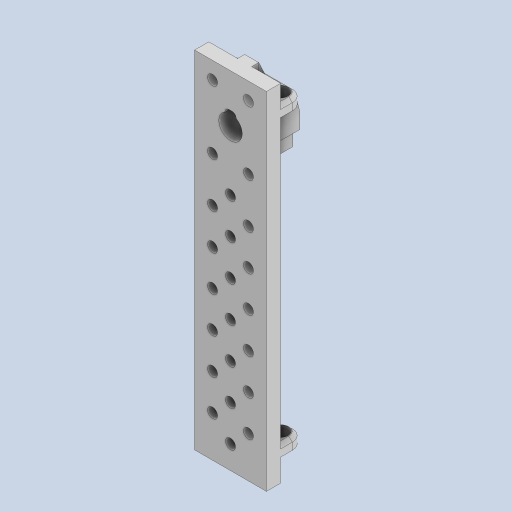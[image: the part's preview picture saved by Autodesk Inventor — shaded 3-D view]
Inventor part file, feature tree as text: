
AUTODESK INVENTOR PART (.ipt)
format: ipt  version: 2024 (Build 280153000, 153)  size: 1,131,520 bytes
history: native  units: mm
features: projected_geometry x31, extrude x23, sketch x19, plane x4, mirror x2, other x2, chamfer x1, loft x1
ambient origin geometry x8: Origin, YZ Plane, XZ Plane, XY Plane, X Axis, Y Axis, Z Axis, Center Point
bodies: Solid1 (feature_tree)
feature tree (83):
  extrude  "Extrusion1"  Depth=10.0mm
  extrude  "Extrusion2"  Depth=16.002mm
  extrude  "Extrusion3"  Depth=16.002mm
  plane  "Work Plane5"
  mirror  "Mirror1"
  extrude  "Extrusion4"  Depth=5.5118mm
  extrude  "Extrusion22"  Depth=2.9972mm
  extrude  "Extrusion23"  Depth=8.001mm
  extrude  "Extrusion24"  Depth=152.5mm
  extrude  "Extrusion14"  Depth=215.0mm
  plane  "Work Plane2"
  extrude  "Extrusion25"  Depth=8.25mm
  chamfer  "Chamfer1"  Distance=1.0mm
  plane  "Work Plane3"
  loft  "Loft6"
  extrude  "Extrusion27"  Depth=10.0mm
  extrude  "Extrusion28"  Depth=10.0mm
  extrude  "Extrusion29"  Depth=10.0mm
  plane  "Work Plane4"
  extrude  "Extrusion30"  Depth=10.0mm
  extrude  "Extrusion31"  Depth=10.0mm
  extrude  "Extrusion32"  Depth=10.0mm
  extrude  "Extrusion33"  Depth=10.0mm
  extrude  "Extrusion34"  Depth=10.0mm
  mirror  "Mirror2"
  extrude  "Extrusion35"  Depth=10.0mm
  extrude  "Extrusion36"  Depth=10.0mm
  extrude  "Extrusion37"  Depth=10.0mm
  sketch  "Sketch40"  dims[d25=1.0mm]
  extrude  "Extrusion38"  Depth=10.0mm
  extrude  "Extrusion39"  Depth=10.0mm
  extrude  "Extrusion40"  Depth=10.0mm
  sketch  "Sketch1"  dims[d0=5.0mm d1=10.0mm]
  projected_geometry  "Projected Loop1"
  projected_geometry  "Projected Loop2"
  projected_geometry  "Projected Loop3"
  projected_geometry  "Projected Loop17"
  sketch  "Sketch23"  dims[d2=122.8852mm d3=16.002mm]
  projected_geometry  "Projected Loop30"
  sketch  "Sketch24"  dims[d4=2.9972mm d5=16.002mm]
  projected_geometry  "Projected Loop31"
  sketch  "Sketch25"  dims[d6=11.938mm d7=5.5118mm]
  projected_geometry  "Projected Loop32"
  sketch  "Sketch26"  dims[d8=5.0038mm d9=2.9972mm]
  projected_geometry  "Projected Loop33"
  other  "Edges11"
  other  "Edges12"
  sketch  "Sketch29"  dims[d10=6.096mm d11=8.001mm]
  projected_geometry  "Projected Loop41"
  projected_geometry  "Projected Loop42"
  projected_geometry  "Projected Loop43"
  projected_geometry  "Projected Loop44"
  projected_geometry  "Projected Loop45"
  projected_geometry  "Projected Loop46"
  sketch  "Sketch30"  dims[d12=6.5mm d13=152.5mm]
  projected_geometry  "Projected Loop47"
  sketch  "Sketch31"  dims[d14=60.0mm d15=215.0mm]
  projected_geometry  "Projected Loop48"
  sketch  "Sketch32"  dims[d16=50.8mm d17=8.25mm]
  projected_geometry  "Projected Loop49"
  sketch  "Sketch33"  dims[d18=16.5mm]
  sketch  "Sketch34"  dims[d19=25.4mm]
  projected_geometry  "Projected Loop50"
  sketch  "Sketch35"  dims[d20=6.35mm]
  projected_geometry  "Projected Loop51"
  sketch  "Sketch36"  dims[d21=127.8852mm]
  projected_geometry  "Projected Loop52"
  sketch  "Sketch37"  dims[d22=10.0076mm]
  projected_geometry  "Projected Loop53"
  projected_geometry  "Projected Loop54"
  sketch  "Sketch38"  dims[d23=20.0mm]
  projected_geometry  "Projected Loop55"
  projected_geometry  "Projected Loop56"
  projected_geometry  "Projected Loop57"
  sketch  "Sketch39"  dims[d24=1.0mm]
  projected_geometry  "Projected Loop58"
  projected_geometry  "Projected Loop59"
  projected_geometry  "Projected Loop60"
  sketch  "Sketch41"  dims[d26=1.0mm]
  projected_geometry  "Projected Loop61"
  projected_geometry  "Projected Loop62"
  sketch  "Sketch44"  dims[d27=1.0mm d28=1.0mm d29=1.0mm d30=1.0mm d31=1.0mm d32=1.0mm d33=1.0mm d34=1.0mm d35=1.0mm d36=1.0mm d37=1.0mm d38=1.0mm d39=1.0mm d40=1.0mm d41=3.0mm d42=3.0mm d43=3.0mm d44=3.0mm d45=3.0mm d46=3.0mm d47=3.0mm d48=3.0mm d49=3.0mm d50=3.0mm d51=3.0mm d52=3.0mm d53=3.0mm d54=3.0mm d55=3.0mm d56=3.0mm d57=3.0mm d58=3.0mm d59=3.0mm d60=3.0mm d61=3.0mm d62=3.0mm d63=3.0mm d64=3.0mm d65=3.0mm d66=3.0mm d67=3.0mm d68=3.0mm d69=3.0mm d70=3.0mm d71=3.0mm d72=3.0mm d73=3.0mm d74=3.0mm d75=3.0mm d76=3.0mm d77=3.0mm d78=3.0mm d79=3.0mm d80=3.0mm d81=3.0mm d82=25.4mm d83=50.8mm d84=245.0mm d86=25.4mm d88=12.7mm d89=12.7mm d90=6.35mm d91=6.35mm d92=12.7mm d93=12.7mm d94=45.0deg d95=45.0deg d96=6.35mm d97=120.0mm d99=25.4mm d100=10.0mm d102=10.0mm d104=10.0mm d105=0.0mm d106=10.0mm d107=13.5128mm d108=10.0mm d109=13.5128mm d110=16.5mm d111=0.0mm d112=16.5mm d113=8.25mm d114=8.25mm d115=16.5mm d116=16.5mm d117=8.25mm d118=6.5mm d119=25.4mm d120=215.0mm d121=0.0mm d122=10.0076mm d123=16.096mm d124=8.048mm d125=184.5mm d126=26.002mm d127=0.0mm d186=50.8mm d187=10.0mm d188=30.4mm d189=0.0mm d190=10.0mm d191=5.0mm d192=0.0mm d196=2.5mm d197=2.0mm d198=45.0deg d236=0.0mm d237=16.096mm d238=26.002mm d239=6.096mm d240=8.001mm d241=6.096mm d242=8.001mm d243=17.0015mm d244=11.096mm d245=0.0mm d246=0.0mm d247=1.0mm d248=0.0mm d249=1.0mm d250=0.0mm d251=3.048mm d252=2.9972mm d257=25.76mm d258=0.0mm d259=0.0mm d260=90.0deg d261=0.0mm d262=90.0deg d269=26.0mm d271=50.8mm d272=25.4mm d273=26.0mm d274=-122.5mm d275=36.0mm d276=0.0mm d277=16.5mm d278=26.0mm d279=26.0mm d280=13.0mm d281=13.0mm d282=13.0mm d283=0.0mm d284=16.5mm d285=16.5mm d286=12.0mm d287=0.0mm d288=0.0mm d290=15.0mm d291=7.5mm d292=13.0mm d293=0.0mm d294=6.0mm d295=3.0mm d296=11.324752mm d297=13.0mm d298=5.662376mm d299=5.663mm d300=0.0mm d301=0.0mm d303=11.0mm d304=-122.5mm d305=68.0mm d306=50.8mm d307=34.0mm d308=10.0mm d309=0.0mm d310=68.0mm d311=34.0mm d312=50.8mm d313=0.0mm d314=6.35mm d318=12.7mm d319=17.0mm d320=20.0mm d322=25.4mm d323=20.0mm d325=45.0mm d328=10.0mm d329=0.0mm d330=22.5mm d331=6.0mm d332=3.0mm d333=0.0mm d334=6.0mm d335=2.0mm d336=0.0mm d337=8.0mm d338=0.0mm d339=0.0mm d340=10.25mm d341=16.5mm d342=3.0mm d343=0.0mm d344=0.0mm d346=6.5mm d348=10.0mm d349=0.0mm d350=15.0mm d351=15.0deg d352=0.0mm d353=0.0mm d354=5.5mm d355=10.5mm d356=10.5mm d357=10.5mm d358=10.5mm d359=10.0mm d360=0.0mm d361=10.0mm d362=0.0mm d364=7.0mm d365=7.0mm d366=7.0mm d367=7.0mm d368=7.0mm d369=7.0mm d370=7.0mm d371=7.0mm d372=7.0mm d373=7.0mm d374=7.0mm d375=7.0mm d376=7.0mm d377=7.0mm d378=7.0mm d379=7.0mm d380=7.0mm d381=7.0mm d382=7.0mm d383=7.0mm d384=7.0mm d385=7.0mm d386=7.0mm d387=10.0mm d388=0.0mm d199=0.872665mm d216=0.5mm d217=0.872665mm d218=0.5mm d219=0.872665mm d228=0.5mm d229=0.872665mm d230=0.5mm d231=0.872665mm]
  projected_geometry  "Projected Loop67"
